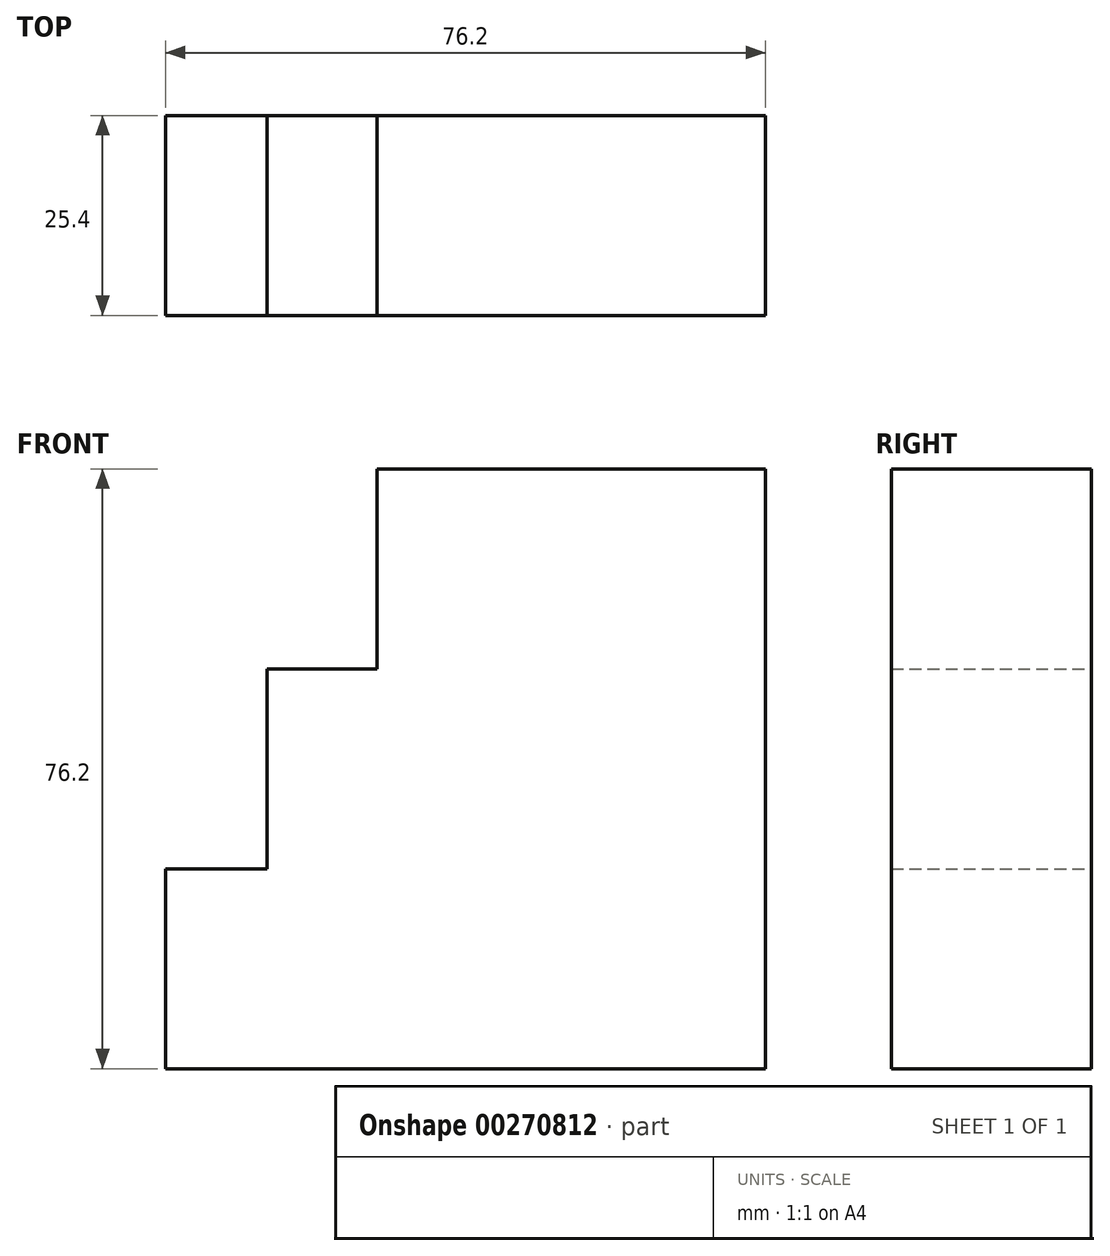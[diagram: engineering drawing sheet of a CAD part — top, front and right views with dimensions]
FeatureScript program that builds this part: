
annotation { "Feature Type Name" : "Feature", "Feature Type Description" : "" }
export const myFeature = defineFeature(function(context is Context, id is Id, definition is map)
    precondition{}
    {
        {
            var Q0;
            Q0=qCreatedBy(makeId("Front.planeOp"),FACE);
            var sketch = newSketch(context, id + "F0", { "sketchPlane" : qUnion([Q0])});
            skLineSegment(sketch, "E0", {"start": v(0, 0) * mm, "end": v(-76.2, 0) * mm});
            skLineSegment(sketch, "E1", {"start": v(-76.2, 0) * mm, "end": v(-76.2, 25.4) * mm});
            skLineSegment(sketch, "E2", {"start": v(-76.2, 25.4) * mm, "end": v(-63.32, 25.4) * mm});
            skLineSegment(sketch, "E3", {"start": v(-63.32, 25.4) * mm, "end": v(-63.32, 50.8) * mm});
            skLineSegment(sketch, "E4", {"start": v(-63.32, 50.8) * mm, "end": v(-49.36, 50.8) * mm});
            skLineSegment(sketch, "E5", {"start": v(-49.36, 50.8) * mm, "end": v(-49.36, 76.2) * mm});
            skLineSegment(sketch, "E6", {"start": v(-49.36, 76.2) * mm, "end": v(0, 76.2) * mm});
            skLineSegment(sketch, "E7", {"start": v(0, 76.2) * mm, "end": v(0, 0) * mm});
            skSolve(sketch);
        }
        {
            var Q0;
            Q0=makeQuery(id+"F0.imprint","IMPRINT",FACE,{"disambiguationData":[TD([[makeQuery(id+"F0.imprint","IMPRINT",EDGE,{"derivedFrom":sQuery(id+"F0.wireOp",EDGE,"E0")}),-1.0]])]});
            extrude(context, id + "F1", {"entities" : qUnion([Q0]), "depth" : 25.4 * mm});
        }
    });
